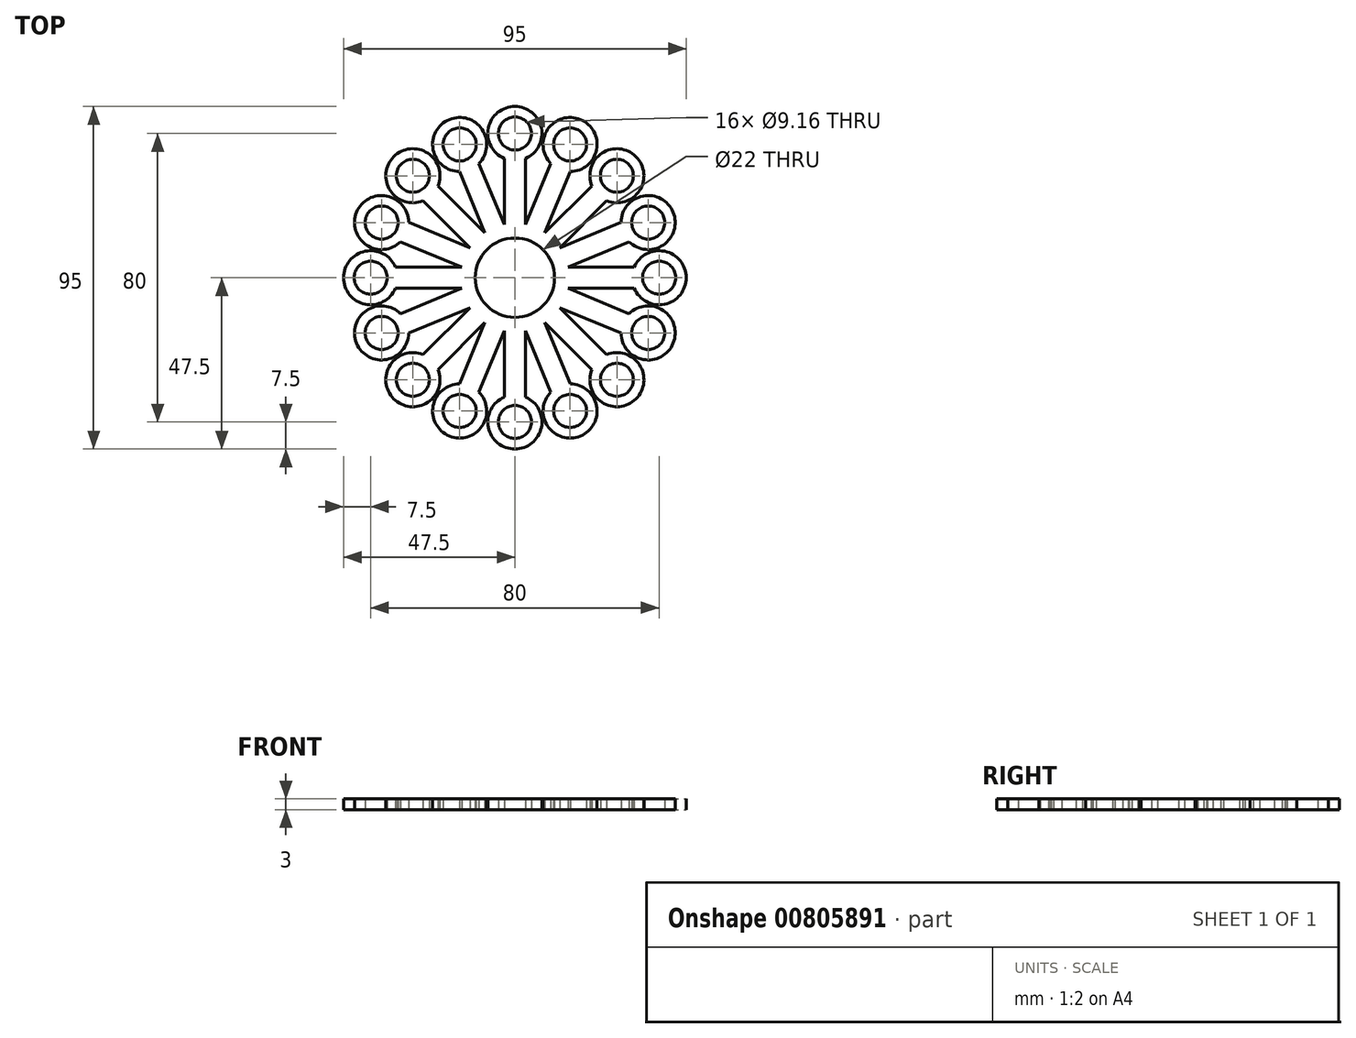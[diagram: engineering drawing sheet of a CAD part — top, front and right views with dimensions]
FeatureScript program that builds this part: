
annotation { "Feature Type Name" : "Feature", "Feature Type Description" : "" }
export const myFeature = defineFeature(function(context is Context, id is Id, definition is map)
    precondition{}
    {
        {
            var Q0;
            Q0=qCreatedBy(makeId("Top.planeOp"),FACE);
            var sketch = newSketch(context, id + "F0", { "sketchPlane" : qUnion([Q0])});
            skArc(sketch, "E0", {"start": v(10.79, -2.15) * mm, "mid": v(11, 0) * mm, "end": v(10.79, 2.15) * mm});
            skCircle(sketch, "E1", {"center": v(40, 0) * mm, "radius": 4.58 * mm});
            skArc(sketch, "E2", {"start": v(33.1, -2.93) * mm, "mid": v(47.5, 0) * mm, "end": v(33.1, 2.93) * mm});
            skPoint(sketch, "E3", {"position": v(14.71, 2.93) * mm});
            skPoint(sketch, "E4", {"position": v(14.71, -2.93) * mm});
            skPoint(sketch, "E5", {"position": v(33.1, 2.93) * mm});
            skPoint(sketch, "E6", {"position": v(33.1, -2.93) * mm});
            skLineSegment(sketch, "E7", {"start": v(14.71, 2.93) * mm, "end": v(33.1, 2.93) * mm});
            skLineSegment(sketch, "E8", {"start": v(14.71, -2.93) * mm, "end": v(33.1, -2.93) * mm});
            skLineSegment(sketch, "E9.1.0", {"start": v(14.71, 2.93) * mm, "end": v(31.7, 9.96) * mm});
            skPoint(sketch, "E9.1.1", {"position": v(12.47, 8.33) * mm});
            skLineSegment(sketch, "E9.1.2", {"start": v(12.47, 8.33) * mm, "end": v(29.46, 15.37) * mm});
            skCircle(sketch, "E9.1.3", {"center": v(36.96, 15.3) * mm, "radius": 4.58 * mm});
            skPoint(sketch, "E9.1.7", {"position": v(29.46, 15.37) * mm});
            skPoint(sketch, "E9.1.8", {"position": v(31.7, 9.96) * mm});
            skArc(sketch, "E9.1.9", {"start": v(31.7, 9.96) * mm, "mid": v(43.88, 18.18) * mm, "end": v(29.46, 15.37) * mm});
            skArc(sketch, "E9.1.10", {"start": v(10.79, 2.15) * mm, "mid": v(10.16, 4.2) * mm, "end": v(9.15, 6.11) * mm});
            skLineSegment(sketch, "E9.2.0", {"start": v(12.47, 8.33) * mm, "end": v(25.47, 21.33) * mm});
            skPoint(sketch, "E9.2.1", {"position": v(8.33, 12.47) * mm});
            skLineSegment(sketch, "E9.2.2", {"start": v(8.33, 12.47) * mm, "end": v(21.33, 25.47) * mm});
            skCircle(sketch, "E9.2.3", {"center": v(28.28, 28.28) * mm, "radius": 4.58 * mm});
            skPoint(sketch, "E9.2.5", {"position": v(12.47, 8.33) * mm});
            skPoint(sketch, "E9.2.7", {"position": v(21.33, 25.47) * mm});
            skPoint(sketch, "E9.2.8", {"position": v(25.47, 21.33) * mm});
            skArc(sketch, "E9.2.9", {"start": v(25.47, 21.33) * mm, "mid": v(33.59, 33.59) * mm, "end": v(21.33, 25.47) * mm});
            skArc(sketch, "E9.2.10", {"start": v(9.15, 6.11) * mm, "mid": v(7.78, 7.78) * mm, "end": v(6.11, 9.15) * mm});
            skLineSegment(sketch, "E9.3.0", {"start": v(8.33, 12.47) * mm, "end": v(15.37, 29.46) * mm});
            skPoint(sketch, "E9.3.1", {"position": v(2.93, 14.71) * mm});
            skLineSegment(sketch, "E9.3.2", {"start": v(2.93, 14.71) * mm, "end": v(9.96, 31.7) * mm});
            skCircle(sketch, "E9.3.3", {"center": v(15.3, 36.96) * mm, "radius": 4.58 * mm});
            skPoint(sketch, "E9.3.5", {"position": v(8.33, 12.47) * mm});
            skPoint(sketch, "E9.3.7", {"position": v(9.96, 31.7) * mm});
            skPoint(sketch, "E9.3.8", {"position": v(15.37, 29.46) * mm});
            skArc(sketch, "E9.3.9", {"start": v(15.37, 29.46) * mm, "mid": v(18.18, 43.88) * mm, "end": v(9.96, 31.7) * mm});
            skArc(sketch, "E9.3.10", {"start": v(6.11, 9.15) * mm, "mid": v(4.2, 10.16) * mm, "end": v(2.15, 10.79) * mm});
            skLineSegment(sketch, "E9.4.0", {"start": v(2.93, 14.71) * mm, "end": v(2.93, 33.1) * mm});
            skPoint(sketch, "E9.4.1", {"position": v(-2.93, 14.71) * mm});
            skLineSegment(sketch, "E9.4.2", {"start": v(-2.93, 14.71) * mm, "end": v(-2.93, 33.1) * mm});
            skCircle(sketch, "E9.4.3", {"center": v(0, 40) * mm, "radius": 4.58 * mm});
            skPoint(sketch, "E9.4.5", {"position": v(2.93, 14.71) * mm});
            skPoint(sketch, "E9.4.7", {"position": v(-2.93, 33.1) * mm});
            skPoint(sketch, "E9.4.8", {"position": v(2.93, 33.1) * mm});
            skArc(sketch, "E9.4.9", {"start": v(2.93, 33.1) * mm, "mid": v(0, 47.5) * mm, "end": v(-2.93, 33.1) * mm});
            skArc(sketch, "E9.4.10", {"start": v(2.15, 10.79) * mm, "mid": v(0, 11) * mm, "end": v(-2.15, 10.79) * mm});
            skLineSegment(sketch, "E9.5.0", {"start": v(-2.93, 14.71) * mm, "end": v(-9.96, 31.7) * mm});
            skPoint(sketch, "E9.5.1", {"position": v(-8.33, 12.47) * mm});
            skLineSegment(sketch, "E9.5.2", {"start": v(-8.33, 12.47) * mm, "end": v(-15.37, 29.46) * mm});
            skCircle(sketch, "E9.5.3", {"center": v(-15.3, 36.96) * mm, "radius": 4.58 * mm});
            skPoint(sketch, "E9.5.5", {"position": v(-2.93, 14.71) * mm});
            skPoint(sketch, "E9.5.7", {"position": v(-15.37, 29.46) * mm});
            skPoint(sketch, "E9.5.8", {"position": v(-9.96, 31.7) * mm});
            skArc(sketch, "E9.5.9", {"start": v(-9.96, 31.7) * mm, "mid": v(-18.18, 43.88) * mm, "end": v(-15.37, 29.46) * mm});
            skArc(sketch, "E9.5.10", {"start": v(-2.15, 10.79) * mm, "mid": v(-4.2, 10.16) * mm, "end": v(-6.11, 9.15) * mm});
            skLineSegment(sketch, "E9.6.0", {"start": v(-8.33, 12.47) * mm, "end": v(-21.33, 25.47) * mm});
            skPoint(sketch, "E9.6.1", {"position": v(-12.47, 8.33) * mm});
            skLineSegment(sketch, "E9.6.2", {"start": v(-12.47, 8.33) * mm, "end": v(-25.47, 21.33) * mm});
            skCircle(sketch, "E9.6.3", {"center": v(-28.28, 28.28) * mm, "radius": 4.58 * mm});
            skPoint(sketch, "E9.6.5", {"position": v(-8.33, 12.47) * mm});
            skPoint(sketch, "E9.6.7", {"position": v(-25.47, 21.33) * mm});
            skPoint(sketch, "E9.6.8", {"position": v(-21.33, 25.47) * mm});
            skArc(sketch, "E9.6.9", {"start": v(-21.33, 25.47) * mm, "mid": v(-33.59, 33.59) * mm, "end": v(-25.47, 21.33) * mm});
            skArc(sketch, "E9.6.10", {"start": v(-6.11, 9.15) * mm, "mid": v(-7.78, 7.78) * mm, "end": v(-9.15, 6.11) * mm});
            skLineSegment(sketch, "E9.7.0", {"start": v(-12.47, 8.33) * mm, "end": v(-29.46, 15.37) * mm});
            skPoint(sketch, "E9.7.1", {"position": v(-14.71, 2.93) * mm});
            skLineSegment(sketch, "E9.7.2", {"start": v(-14.71, 2.93) * mm, "end": v(-31.7, 9.96) * mm});
            skCircle(sketch, "E9.7.3", {"center": v(-36.96, 15.3) * mm, "radius": 4.58 * mm});
            skPoint(sketch, "E9.7.5", {"position": v(-12.47, 8.33) * mm});
            skPoint(sketch, "E9.7.7", {"position": v(-31.7, 9.96) * mm});
            skPoint(sketch, "E9.7.8", {"position": v(-29.46, 15.37) * mm});
            skArc(sketch, "E9.7.9", {"start": v(-29.46, 15.37) * mm, "mid": v(-43.88, 18.18) * mm, "end": v(-31.7, 9.96) * mm});
            skArc(sketch, "E9.7.10", {"start": v(-9.15, 6.11) * mm, "mid": v(-10.16, 4.2) * mm, "end": v(-10.79, 2.15) * mm});
            skLineSegment(sketch, "E9.8.0", {"start": v(-14.71, 2.93) * mm, "end": v(-33.1, 2.93) * mm});
            skPoint(sketch, "E9.8.1", {"position": v(-14.71, -2.93) * mm});
            skLineSegment(sketch, "E9.8.2", {"start": v(-14.71, -2.93) * mm, "end": v(-33.1, -2.93) * mm});
            skCircle(sketch, "E9.8.3", {"center": v(-40, 0) * mm, "radius": 4.58 * mm});
            skPoint(sketch, "E9.8.5", {"position": v(-14.71, 2.93) * mm});
            skPoint(sketch, "E9.8.7", {"position": v(-33.1, -2.93) * mm});
            skPoint(sketch, "E9.8.8", {"position": v(-33.1, 2.93) * mm});
            skArc(sketch, "E9.8.9", {"start": v(-33.1, 2.93) * mm, "mid": v(-47.5, 0) * mm, "end": v(-33.1, -2.93) * mm});
            skArc(sketch, "E9.8.10", {"start": v(-10.79, 2.15) * mm, "mid": v(-11, 0) * mm, "end": v(-10.79, -2.15) * mm});
            skLineSegment(sketch, "E9.9.0", {"start": v(-14.71, -2.93) * mm, "end": v(-31.7, -9.96) * mm});
            skPoint(sketch, "E9.9.1", {"position": v(-12.47, -8.33) * mm});
            skLineSegment(sketch, "E9.9.2", {"start": v(-12.47, -8.33) * mm, "end": v(-29.46, -15.37) * mm});
            skCircle(sketch, "E9.9.3", {"center": v(-36.96, -15.3) * mm, "radius": 4.58 * mm});
            skPoint(sketch, "E9.9.5", {"position": v(-14.71, -2.93) * mm});
            skPoint(sketch, "E9.9.7", {"position": v(-29.46, -15.37) * mm});
            skPoint(sketch, "E9.9.8", {"position": v(-31.7, -9.96) * mm});
            skArc(sketch, "E9.9.9", {"start": v(-31.7, -9.96) * mm, "mid": v(-43.88, -18.18) * mm, "end": v(-29.46, -15.37) * mm});
            skArc(sketch, "E9.9.10", {"start": v(-10.79, -2.15) * mm, "mid": v(-10.16, -4.2) * mm, "end": v(-9.15, -6.11) * mm});
            skLineSegment(sketch, "E9.10.0", {"start": v(-12.47, -8.33) * mm, "end": v(-25.47, -21.33) * mm});
            skPoint(sketch, "E9.10.1", {"position": v(-8.33, -12.47) * mm});
            skLineSegment(sketch, "E9.10.2", {"start": v(-8.33, -12.47) * mm, "end": v(-21.33, -25.47) * mm});
            skCircle(sketch, "E9.10.3", {"center": v(-28.28, -28.28) * mm, "radius": 4.58 * mm});
            skPoint(sketch, "E9.10.5", {"position": v(-12.47, -8.33) * mm});
            skPoint(sketch, "E9.10.7", {"position": v(-21.33, -25.47) * mm});
            skPoint(sketch, "E9.10.8", {"position": v(-25.47, -21.33) * mm});
            skArc(sketch, "E9.10.9", {"start": v(-25.47, -21.33) * mm, "mid": v(-33.59, -33.59) * mm, "end": v(-21.33, -25.47) * mm});
            skArc(sketch, "E9.10.10", {"start": v(-9.15, -6.11) * mm, "mid": v(-7.78, -7.78) * mm, "end": v(-6.11, -9.15) * mm});
            skLineSegment(sketch, "E9.11.0", {"start": v(-8.33, -12.47) * mm, "end": v(-15.37, -29.46) * mm});
            skPoint(sketch, "E9.11.1", {"position": v(-2.93, -14.71) * mm});
            skLineSegment(sketch, "E9.11.2", {"start": v(-2.93, -14.71) * mm, "end": v(-9.96, -31.7) * mm});
            skCircle(sketch, "E9.11.3", {"center": v(-15.3, -36.96) * mm, "radius": 4.58 * mm});
            skPoint(sketch, "E9.11.5", {"position": v(-8.33, -12.47) * mm});
            skPoint(sketch, "E9.11.7", {"position": v(-9.96, -31.7) * mm});
            skPoint(sketch, "E9.11.8", {"position": v(-15.37, -29.46) * mm});
            skArc(sketch, "E9.11.9", {"start": v(-15.37, -29.46) * mm, "mid": v(-18.18, -43.88) * mm, "end": v(-9.96, -31.7) * mm});
            skArc(sketch, "E9.11.10", {"start": v(-6.11, -9.15) * mm, "mid": v(-4.2, -10.16) * mm, "end": v(-2.15, -10.79) * mm});
            skLineSegment(sketch, "E9.12.0", {"start": v(-2.93, -14.71) * mm, "end": v(-2.93, -33.1) * mm});
            skPoint(sketch, "E9.12.1", {"position": v(2.93, -14.71) * mm});
            skLineSegment(sketch, "E9.12.2", {"start": v(2.93, -14.71) * mm, "end": v(2.93, -33.1) * mm});
            skCircle(sketch, "E9.12.3", {"center": v(0, -40) * mm, "radius": 4.58 * mm});
            skPoint(sketch, "E9.12.5", {"position": v(-2.93, -14.71) * mm});
            skPoint(sketch, "E9.12.7", {"position": v(2.93, -33.1) * mm});
            skPoint(sketch, "E9.12.8", {"position": v(-2.93, -33.1) * mm});
            skArc(sketch, "E9.12.9", {"start": v(-2.93, -33.1) * mm, "mid": v(0, -47.5) * mm, "end": v(2.93, -33.1) * mm});
            skArc(sketch, "E9.12.10", {"start": v(-2.15, -10.79) * mm, "mid": v(0, -11) * mm, "end": v(2.15, -10.79) * mm});
            skLineSegment(sketch, "E9.13.0", {"start": v(2.93, -14.71) * mm, "end": v(9.96, -31.7) * mm});
            skPoint(sketch, "E9.13.1", {"position": v(8.33, -12.47) * mm});
            skLineSegment(sketch, "E9.13.2", {"start": v(8.33, -12.47) * mm, "end": v(15.37, -29.46) * mm});
            skCircle(sketch, "E9.13.3", {"center": v(15.3, -36.96) * mm, "radius": 4.58 * mm});
            skPoint(sketch, "E9.13.5", {"position": v(2.93, -14.71) * mm});
            skPoint(sketch, "E9.13.7", {"position": v(15.37, -29.46) * mm});
            skPoint(sketch, "E9.13.8", {"position": v(9.96, -31.7) * mm});
            skArc(sketch, "E9.13.9", {"start": v(9.96, -31.7) * mm, "mid": v(18.18, -43.88) * mm, "end": v(15.37, -29.46) * mm});
            skArc(sketch, "E9.13.10", {"start": v(2.15, -10.79) * mm, "mid": v(4.2, -10.16) * mm, "end": v(6.11, -9.15) * mm});
            skLineSegment(sketch, "E9.14.0", {"start": v(8.33, -12.47) * mm, "end": v(21.33, -25.47) * mm});
            skPoint(sketch, "E9.14.1", {"position": v(12.47, -8.33) * mm});
            skLineSegment(sketch, "E9.14.2", {"start": v(12.47, -8.33) * mm, "end": v(25.47, -21.33) * mm});
            skCircle(sketch, "E9.14.3", {"center": v(28.28, -28.28) * mm, "radius": 4.58 * mm});
            skPoint(sketch, "E9.14.5", {"position": v(8.33, -12.47) * mm});
            skPoint(sketch, "E9.14.7", {"position": v(25.47, -21.33) * mm});
            skPoint(sketch, "E9.14.8", {"position": v(21.33, -25.47) * mm});
            skArc(sketch, "E9.14.9", {"start": v(21.33, -25.47) * mm, "mid": v(33.59, -33.59) * mm, "end": v(25.47, -21.33) * mm});
            skArc(sketch, "E9.14.10", {"start": v(6.11, -9.15) * mm, "mid": v(7.78, -7.78) * mm, "end": v(9.15, -6.11) * mm});
            skLineSegment(sketch, "E9.15.0", {"start": v(12.47, -8.33) * mm, "end": v(29.46, -15.37) * mm});
            skLineSegment(sketch, "E9.15.2", {"start": v(14.71, -2.93) * mm, "end": v(31.7, -9.96) * mm});
            skCircle(sketch, "E9.15.3", {"center": v(36.96, -15.3) * mm, "radius": 4.58 * mm});
            skPoint(sketch, "E9.15.5", {"position": v(12.47, -8.33) * mm});
            skPoint(sketch, "E9.15.7", {"position": v(31.7, -9.96) * mm});
            skPoint(sketch, "E9.15.8", {"position": v(29.46, -15.37) * mm});
            skArc(sketch, "E9.15.9", {"start": v(29.46, -15.37) * mm, "mid": v(43.88, -18.18) * mm, "end": v(31.7, -9.96) * mm});
            skArc(sketch, "E9.15.10", {"start": v(9.15, -6.11) * mm, "mid": v(10.16, -4.2) * mm, "end": v(10.79, -2.15) * mm});
            skSolve(sketch);
        }
        {
            var Q0;
            Q0 = qSketchRegion(id + "F0", true);
            extrude(context, id + "F1", {"entities" : qUnion([Q0]), "depth" : 3 * mm, "offsetDistance" : 25 * mm});
        }
    });
